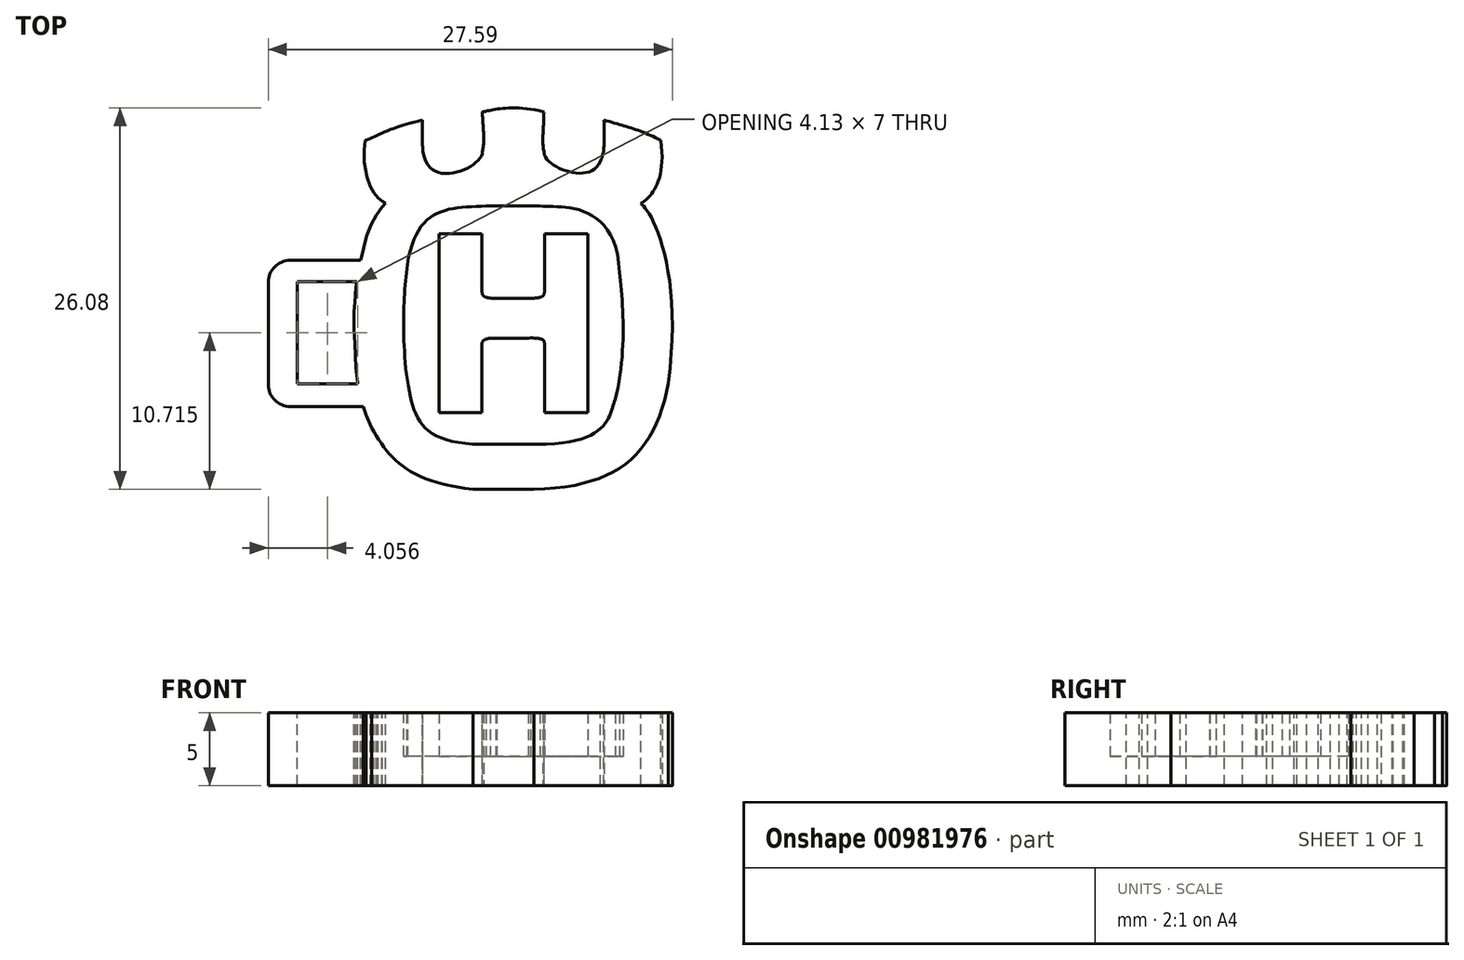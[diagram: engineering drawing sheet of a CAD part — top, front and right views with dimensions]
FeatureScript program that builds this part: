
annotation { "Feature Type Name" : "Feature", "Feature Type Description" : "" }
export const myFeature = defineFeature(function(context is Context, id is Id, definition is map)
    precondition{}
    {
        {
            var Q0;
            Q0=qCreatedBy(makeId("Top.planeOp"),FACE);
            var sketch = newSketch(context, id + "F0", { "sketchPlane" : qUnion([Q0])});
            skLineSegment(sketch, "E0", {"start": v(24.3, 30.4) * mm, "end": v(27.25, 30.4) * mm});
            skLineSegment(sketch, "E1", {"start": v(27.25, 30.4) * mm, "end": v(27.25, 26.4) * mm});
            skLineSegment(sketch, "E2", {"start": v(24.3, 30.4) * mm, "end": v(24.3, 18.18) * mm});
            skLineSegment(sketch, "E3", {"start": v(24.3, 18.18) * mm, "end": v(27.25, 18.18) * mm});
            skLineSegment(sketch, "E4", {"start": v(27.25, 18.18) * mm, "end": v(27.25, 22.8) * mm});
            skLineSegment(sketch, "E5", {"start": v(31.53, 30.4) * mm, "end": v(34.47, 30.4) * mm});
            skLineSegment(sketch, "E6", {"start": v(34.47, 30.4) * mm, "end": v(34.47, 18.18) * mm});
            skLineSegment(sketch, "E7", {"start": v(34.47, 18.18) * mm, "end": v(31.52, 18.18) * mm});
            skLineSegment(sketch, "E8", {"start": v(31.52, 18.18) * mm, "end": v(31.52, 22.83) * mm});
            skLineSegment(sketch, "E9", {"start": v(31.53, 30.4) * mm, "end": v(31.53, 26.45) * mm});
            skFitSpline(sketch, "E10", {"points": [v(27.25, 22.8) * mm, v(28.26, 23.27) * mm], "startDerivative": vector(0.02, 0.7) * mm, "endDerivative": vector(3.13, -0.07) * mm});
            skFitSpline(sketch, "E11", {"points": [v(31.52, 22.83) * mm, v(30.4, 23.27) * mm], "startDerivative": vector(-0.12, 0.69) * mm, "endDerivative": vector(-3.63, -0.1) * mm});
            skLineSegment(sketch, "E12", {"start": v(28.26, 23.27) * mm, "end": v(30.4, 23.27) * mm});
            skFitSpline(sketch, "E13", {"points": [v(27.54, 32.3) * mm, v(22.15, 28.29) * mm], "startDerivative": vector(-8.02, -0.26) * mm, "endDerivative": vector(-1.8, -11.85) * mm});
            skLineSegment(sketch, "E14", {"start": v(27.54, 32.3) * mm, "end": v(31.2, 32.3) * mm});
            skFitSpline(sketch, "E15", {"points": [v(31.2, 32.3) * mm, v(36.64, 27.77) * mm], "startDerivative": vector(4.03, -0.34) * mm, "endDerivative": vector(0.81, -15.1) * mm});
            skFitSpline(sketch, "E16", {"points": [v(36.64, 27.77) * mm, v(36.33, 19.1) * mm], "startDerivative": vector(0.7, -6.35) * mm, "endDerivative": vector(-2.47, -9.34) * mm});
            skFitSpline(sketch, "E17", {"points": [v(36.33, 19.1) * mm, v(31, 16.02) * mm], "startDerivative": vector(-1.08, -2.93) * mm, "endDerivative": vector(-15.21, 0.1) * mm});
            skLineSegment(sketch, "E18", {"start": v(31, 16.02) * mm, "end": v(27.8, 16.02) * mm});
            skFitSpline(sketch, "E19", {"points": [v(27.8, 16.02) * mm, v(22.09, 20.78) * mm], "startDerivative": vector(-14.76, -0.3) * mm, "endDerivative": vector(-1.43, 8.98) * mm});
            skFitSpline(sketch, "E20", {"points": [v(22.15, 28.29) * mm, v(22.09, 20.78) * mm], "startDerivative": vector(-0.75, -6.25) * mm, "endDerivative": vector(1.04, -9.62) * mm});
            skLineSegment(sketch, "E21", {"start": v(19.28, 36.78) * mm, "end": v(19.22, 36.1) * mm});
            skLineSegment(sketch, "E22", {"start": v(19.22, 36.1) * mm, "end": v(19.22, 35.5) * mm});
            skLineSegment(sketch, "E23", {"start": v(19.22, 35.5) * mm, "end": v(19.22, 35.29) * mm});
            skLineSegment(sketch, "E24", {"start": v(19.22, 35.29) * mm, "end": v(19.38, 34.28) * mm});
            skLineSegment(sketch, "E25", {"start": v(19.38, 34.28) * mm, "end": v(19.61, 33.64) * mm});
            skLineSegment(sketch, "E26", {"start": v(19.61, 33.64) * mm, "end": v(19.87, 33.2) * mm});
            skLineSegment(sketch, "E27", {"start": v(19.87, 33.2) * mm, "end": v(20.15, 32.85) * mm});
            skLineSegment(sketch, "E28", {"start": v(20.15, 32.85) * mm, "end": v(20.43, 32.62) * mm});
            skLineSegment(sketch, "E29", {"start": v(20.43, 32.62) * mm, "end": v(20.66, 32.49) * mm});
            skLineSegment(sketch, "E30", {"start": v(20.66, 32.49) * mm, "end": v(20.42, 32.21) * mm});
            skLineSegment(sketch, "E31", {"start": v(20.42, 32.21) * mm, "end": v(20.03, 31.67) * mm});
            skLineSegment(sketch, "E32", {"start": v(20.03, 31.67) * mm, "end": v(19.7, 31.05) * mm});
            skLineSegment(sketch, "E33", {"start": v(19.7, 31.05) * mm, "end": v(19.38, 30.23) * mm});
            skLineSegment(sketch, "E34", {"start": v(19.38, 30.23) * mm, "end": v(19.16, 29.46) * mm});
            skLineSegment(sketch, "E35", {"start": v(19.16, 29.46) * mm, "end": v(19, 28.77) * mm});
            skLineSegment(sketch, "E36", {"start": v(19, 28.77) * mm, "end": v(18.92, 28.4) * mm});
            skLineSegment(sketch, "E37", {"start": v(18.92, 28.4) * mm, "end": v(18.88, 28.2) * mm});
            skLineSegment(sketch, "E38", {"start": v(18.88, 28.2) * mm, "end": v(18.75, 27.52) * mm});
            skLineSegment(sketch, "E39", {"start": v(18.75, 27.52) * mm, "end": v(18.65, 26.73) * mm});
            skLineSegment(sketch, "E40", {"start": v(18.65, 26.73) * mm, "end": v(18.56, 25.73) * mm});
            skLineSegment(sketch, "E41", {"start": v(18.56, 25.73) * mm, "end": v(18.5, 25.06) * mm});
            skLineSegment(sketch, "E42", {"start": v(18.5, 25.06) * mm, "end": v(18.5, 23.82) * mm});
            skLineSegment(sketch, "E43", {"start": v(18.5, 23.82) * mm, "end": v(18.56, 22.9) * mm});
            skLineSegment(sketch, "E44", {"start": v(18.56, 22.9) * mm, "end": v(18.64, 21.24) * mm});
            skLineSegment(sketch, "E45", {"start": v(18.64, 21.24) * mm, "end": v(18.75, 20.25) * mm});
            skLineSegment(sketch, "E46", {"start": v(18.75, 20.25) * mm, "end": v(18.97, 19.15) * mm});
            skLineSegment(sketch, "E47", {"start": v(18.97, 19.15) * mm, "end": v(19.34, 18.01) * mm});
            skLineSegment(sketch, "E48", {"start": v(19.34, 18.01) * mm, "end": v(19.7, 17.14) * mm});
            skFitSpline(sketch, "E49", {"points": [v(19.7, 17.14) * mm, v(26.63, 12.93) * mm], "startDerivative": vector(3.77, -6.54) * mm, "endDerivative": vector(13.37, -1.64) * mm});
            skLineSegment(sketch, "E50", {"start": v(26.63, 12.93) * mm, "end": v(30.8, 12.93) * mm});
            skFitSpline(sketch, "E51", {"points": [v(30.8, 12.93) * mm, v(39.97, 20.2) * mm], "startDerivative": vector(17.5, 0.44) * mm, "endDerivative": vector(2.7, 14.34) * mm});
            skFitSpline(sketch, "E52", {"points": [v(39.97, 20.2) * mm, v(38.09, 32.46) * mm], "startDerivative": vector(3.17, 24.6) * mm, "endDerivative": vector(-1.72, 0.88) * mm});
            skFitSpline(sketch, "E53", {"points": [v(38.09, 32.46) * mm, v(39.46, 36.8) * mm], "startDerivative": vector(1.01, 0.72) * mm, "endDerivative": vector(-1.3, 9.58) * mm});
            skFitSpline(sketch, "E54", {"points": [v(39.46, 36.8) * mm, v(35.57, 38.18) * mm], "startDerivative": vector(-4.41, 2.21) * mm, "endDerivative": vector(-4.46, 1.23) * mm});
            skFitSpline(sketch, "E55", {"points": [v(35.57, 38.18) * mm, v(35.33, 35.35) * mm], "startDerivative": vector(0.08, -3.07) * mm, "endDerivative": vector(-1.05, -1.85) * mm});
            skFitSpline(sketch, "E56", {"points": [v(35.33, 35.35) * mm, v(31.47, 36.03) * mm], "startDerivative": vector(-2.17, -5.19) * mm, "endDerivative": vector(0.45, 2.97) * mm});
            skFitSpline(sketch, "E57", {"points": [v(31.47, 36.03) * mm, v(31.47, 38.73) * mm], "startDerivative": vector(-0.49, 2.12) * mm, "endDerivative": vector(0, 2.7) * mm});
            skFitSpline(sketch, "E58", {"points": [v(31.47, 38.73) * mm, v(27.27, 38.73) * mm], "startDerivative": vector(-7.36, 1.8) * mm, "endDerivative": vector(-0.94, -0.06) * mm});
            skFitSpline(sketch, "E59", {"points": [v(27.27, 38.73) * mm, v(27.27, 36) * mm], "startDerivative": vector(0.13, -3.05) * mm, "endDerivative": vector(-0.58, -2.37) * mm});
            skFitSpline(sketch, "E60", {"points": [v(27.27, 36) * mm, v(23.22, 36) * mm], "startDerivative": vector(0.16, -3.18) * mm, "endDerivative": vector(-1.08, 8.2) * mm});
            skFitSpline(sketch, "E61", {"points": [v(23.22, 36) * mm, v(23.17, 38.18) * mm], "startDerivative": vector(-0.22, 1.88) * mm, "endDerivative": vector(-0.05, 1.94) * mm});
            skFitSpline(sketch, "E62", {"points": [v(19.28, 36.78) * mm, v(23.17, 38.18) * mm], "startDerivative": vector(4.11, 1.72) * mm, "endDerivative": vector(7.33, 1.9) * mm});
            skLineSegment(sketch, "E63.bottom", {"start": v(19.65, 28.6) * mm, "end": v(12.65, 28.6) * mm});
            skLineSegment(sketch, "E63.top", {"start": v(19.65, 18.6) * mm, "end": v(12.65, 18.6) * mm});
            skLineSegment(sketch, "E63.left", {"start": v(19.65, 28.6) * mm, "end": v(19.65, 18.6) * mm});
            skLineSegment(sketch, "E63.right", {"start": v(12.65, 28.6) * mm, "end": v(12.65, 18.6) * mm});
            skLineSegment(sketch, "E64.bottom", {"start": v(19.64, 27.15) * mm, "end": v(14.64, 27.15) * mm});
            skLineSegment(sketch, "E64.top", {"start": v(19.64, 20.15) * mm, "end": v(14.64, 20.15) * mm});
            skLineSegment(sketch, "E64.left", {"start": v(19.64, 27.15) * mm, "end": v(19.64, 20.15) * mm});
            skLineSegment(sketch, "E64.right", {"start": v(14.64, 27.15) * mm, "end": v(14.64, 20.15) * mm});
            skFitSpline(sketch, "E65", {"points": [v(27.25, 26.4) * mm, v(28.18, 26) * mm], "startDerivative": vector(0.06, -0.44) * mm, "endDerivative": vector(2.71, 0.13) * mm});
            skFitSpline(sketch, "E66", {"points": [v(31.53, 26.45) * mm, v(30.56, 26) * mm], "startDerivative": vector(-0.25, -0.7) * mm, "endDerivative": vector(-3.03, -0.05) * mm});
            skLineSegment(sketch, "E67", {"start": v(28.18, 26) * mm, "end": v(30.56, 26) * mm});
            skSolve(sketch);
        }
        {
            var Q0;
            Q0=makeQuery(id+"F0.imprint","IMPRINT",FACE,{"disambiguationData":[TD([[makeQuery(id+"F0.imprint","IMPRINT",EDGE,{"derivedFrom":sQuery(id+"F0.wireOp",EDGE,"E13")}),-1.0]])]});
            var Q1;
            Q1=makeQuery(id+"F0.imprint","IMPRINT",FACE,{"disambiguationData":[TD([[makeQuery(id+"F0.imprint","IMPRINT",EDGE,{"derivedFrom":sQuery(id+"F0.wireOp",EDGE,"E0")}),1.0]])]});
            var Q2;
            Q2=makeQuery(id+"F0.imprint","IMPRINT",FACE,{"disambiguationData":[TD([[makeQuery(id+"F0.imprint","IMPRINT",EDGE,{"derivedFrom":sQuery(id+"F0.wireOp",EDGE,"E0")}),-1.0]])]});
            var Q3;
            {var subQ11=sQuery(id+"F0.wireOp",EDGE,"E37");Q3=makeQuery(id+"F0.imprint","IMPRINT",FACE,{"disambiguationData":[TD([[makeQuery(id+"F0.imprint","IMPRINT",EDGE,{"derivedFrom":subQ11}),-1.0]])]});}
            var Q4;
            {var subQ7=sQuery(id+"F0.wireOp",EDGE,"E37");Q4=makeQuery(id+"F0.imprint","IMPRINT",FACE,{"disambiguationData":[TD([[makeQuery(id+"F0.imprint","IMPRINT",EDGE,{"derivedFrom":subQ7}),1.0]])]});}
            var Q5;
            {var subQ8=sQuery(id+"F0.wireOp",EDGE,"E40");Q5=makeQuery(id+"F0.imprint","IMPRINT",FACE,{"disambiguationData":[TD([[makeQuery(id+"F0.imprint","IMPRINT",EDGE,{"derivedFrom":subQ8}),1.0]])]});}
            extrude(context, id + "F1", {"entities" : qUnion([Q0, Q1, Q2, Q3, Q4, Q5]), "depth" : 0 * mm, "offsetDistance" : 25 * mm, "hasSecondDirection" : true, "secondDirectionOppositeDirection" : true, "secondDirectionDepth" : 2 * mm});
        }
        {
            var Q0;
            Q0=makeQuery(id+"F0.imprint","IMPRINT",FACE,{"disambiguationData":[TD([[makeQuery(id+"F0.imprint","IMPRINT",EDGE,{"derivedFrom":sQuery(id+"F0.wireOp",EDGE,"E13")}),-1.0]])]});
            var Q1;
            {var subQ7=sQuery(id+"F0.wireOp",EDGE,"E37");Q1=makeQuery(id+"F0.imprint","IMPRINT",FACE,{"disambiguationData":[TD([[makeQuery(id+"F0.imprint","IMPRINT",EDGE,{"derivedFrom":subQ7}),1.0]])]});}
            var Q2;
            {var subQ8=sQuery(id+"F0.wireOp",EDGE,"E40");Q2=makeQuery(id+"F0.imprint","IMPRINT",FACE,{"disambiguationData":[TD([[makeQuery(id+"F0.imprint","IMPRINT",EDGE,{"derivedFrom":subQ8}),1.0]])]});}
            var Q3;
            {var subQ11=sQuery(id+"F0.wireOp",EDGE,"E37");Q3=makeQuery(id+"F0.imprint","IMPRINT",FACE,{"disambiguationData":[TD([[makeQuery(id+"F0.imprint","IMPRINT",EDGE,{"derivedFrom":subQ11}),-1.0]])]});}
            var Q4;
            Q4=makeQuery(id+"F0.imprint","IMPRINT",FACE,{"disambiguationData":[TD([[makeQuery(id+"F0.imprint","IMPRINT",EDGE,{"derivedFrom":sQuery(id+"F0.wireOp",EDGE,"E0")}),-1.0]])]});
            extrude(context, id + "F2", {"entities" : qUnion([Q0, Q1, Q2, Q3, Q4]), "operationType" : NewBodyOperationType.ADD, "depth" : 3 * mm, "offsetDistance" : 25 * mm});
        }
        {
            var Q0;
            {var subQ0=sQuery(id+"F0.wireOp",EDGE,"E63.right");var subQ1=sQuery(id+"F0.wireOp",EDGE,"E63.top");Q0=makeQuery(id+"F2.boolean.opBoolean","MERGE",EDGE,{"derivedFrom":[makeQuery(id+"F1.opExtrude","SWEPT_EDGE",EDGE,{"disambiguationData":[OSD([subQ1,subQ0])]}),makeQuery(id+"F2.opExtrude","SWEPT_EDGE",EDGE,{"disambiguationData":[OSD([subQ1,subQ0])]})]});}
            var Q1;
            {var subQ0=sQuery(id+"F0.wireOp",EDGE,"E63.right");var subQ1=sQuery(id+"F0.wireOp",EDGE,"E63.bottom");Q1=makeQuery(id+"F2.boolean.opBoolean","MERGE",EDGE,{"derivedFrom":[makeQuery(id+"F1.opExtrude","SWEPT_EDGE",EDGE,{"disambiguationData":[OSD([subQ1,subQ0])]}),makeQuery(id+"F2.opExtrude","SWEPT_EDGE",EDGE,{"disambiguationData":[OSD([subQ1,subQ0])]})]});}
            fillet(context, id + "F3", {"entities" : qUnion([Q0, Q1]), "radius" : 1.5 * mm, "tangentPropagation" : true, "allowEdgeOverflow" : false});
        }
    });
